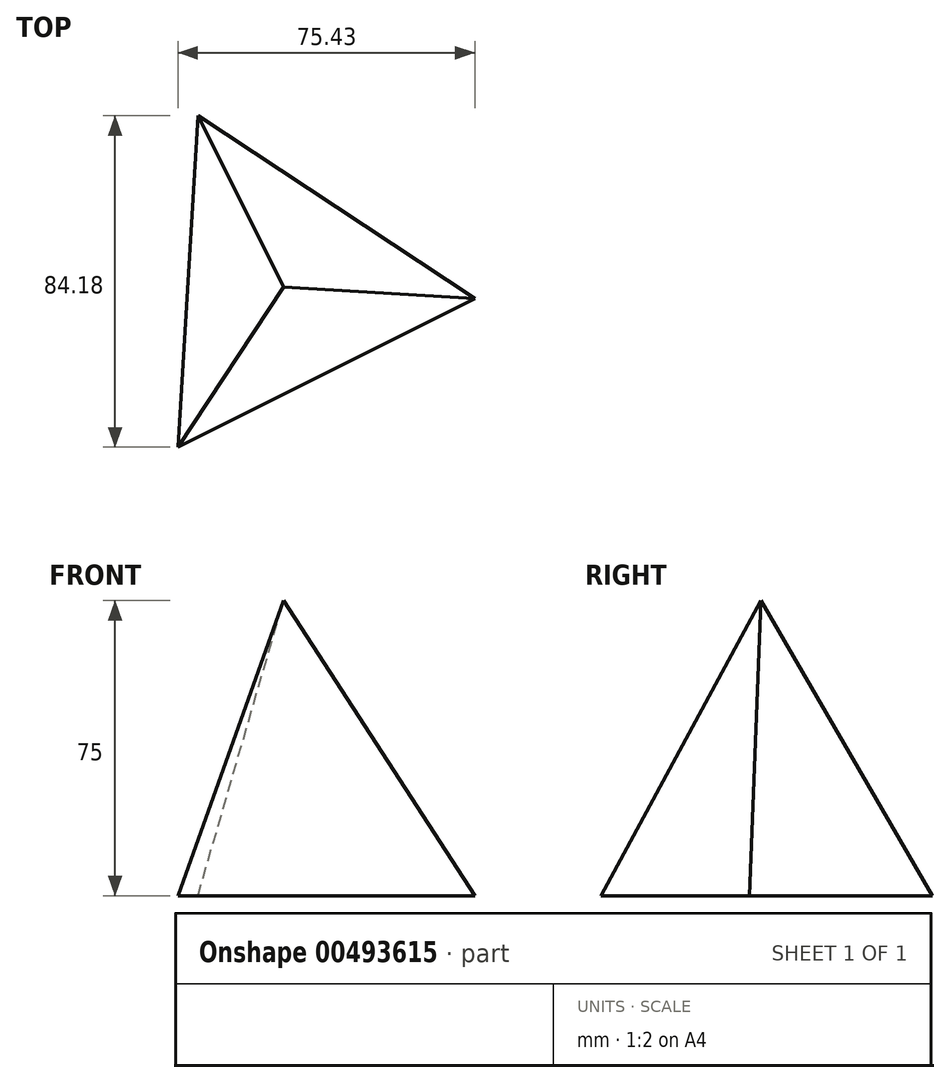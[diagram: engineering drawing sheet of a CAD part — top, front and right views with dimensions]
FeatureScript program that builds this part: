
annotation { "Feature Type Name" : "Feature", "Feature Type Description" : "" }
export const myFeature = defineFeature(function(context is Context, id is Id, definition is map)
    precondition{}
    {
        {
            var Q0;
            Q0=qCreatedBy(makeId("Top.planeOp"),FACE);
            var sketch = newSketch(context, id + "F0", { "sketchPlane" : qUnion([Q0])});
            skCircle(sketch, "E0.cCircle", {"center": v(0, 0) * mm, "radius": 48.7 * mm, "construction": true});
            skLineSegment(sketch, "E0.0", {"start": v(-26.83, -40.63) * mm, "end": v(-21.78, 43.55) * mm});
            skLineSegment(sketch, "E0.1", {"start": v(-21.78, 43.55) * mm, "end": v(48.6, -2.92) * mm});
            skLineSegment(sketch, "E0.2", {"start": v(48.6, -2.92) * mm, "end": v(-26.83, -40.63) * mm});
            skSolve(sketch);
        }
        {
            var Q0;
            Q0=qCreatedBy(makeId("Top.planeOp"),FACE);
            cPlane(context, id + "F1", {"entities" : qUnion([Q0]), "cplaneType" : CPlaneType.OFFSET, "offset" : 75 * mm, "width" : 150 * mm, "height" : 150 * mm});
        }
        {
            var Q0;
            Q0=qCreatedBy(id+"F1.planeOp",FACE);
            var sketch = newSketch(context, id + "F2", { "sketchPlane" : qUnion([Q0])});
            skPoint(sketch, "E1", {"position": v(0, 0) * mm});
            skSolve(sketch);
        }
        {
            var Q0;
            Q0=makeQuery(id+"F0.imprint","IMPRINT",FACE,{"disambiguationData":[TD([[makeQuery(id+"F0.imprint","IMPRINT",EDGE,{"derivedFrom":sQuery(id+"F0.wireOp",EDGE,"E0.0")}),-1.0]])]});
            var Q1;
            Q1=sQuery(id+"F2.wireOp",VERTEX,"E1");
            loft(context, id + "F3", {"sheetProfilesArray" : [{ "sheetProfileEntities" : qUnion([Q0]) }, { "sheetProfileEntities" : qUnion([Q1]) }]});
        }
    });
